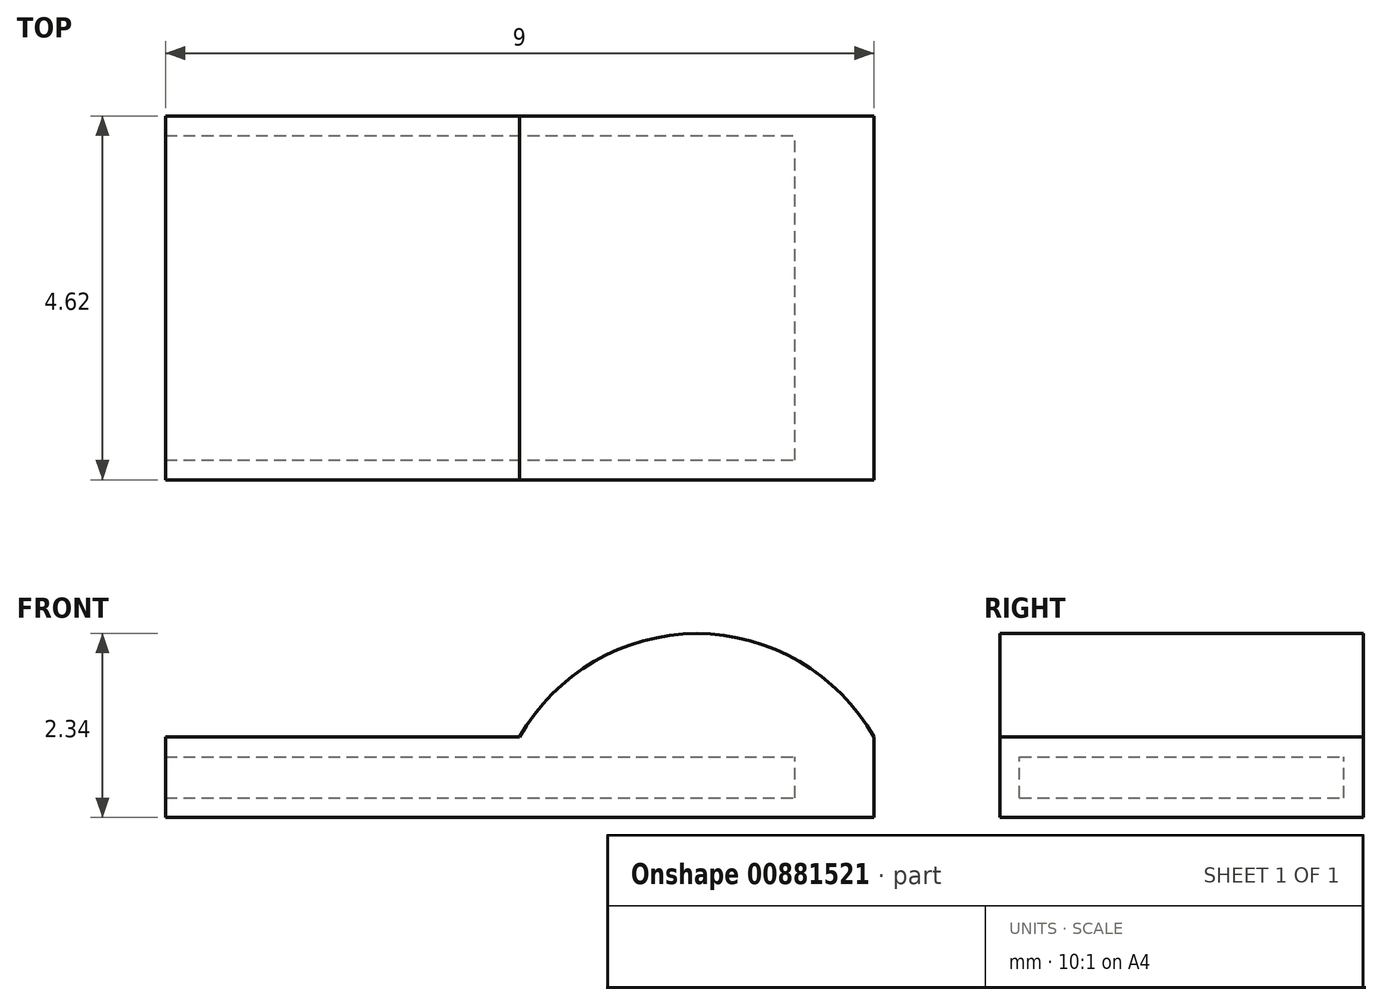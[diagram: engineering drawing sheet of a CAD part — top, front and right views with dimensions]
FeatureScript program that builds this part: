
annotation { "Feature Type Name" : "Feature", "Feature Type Description" : "" }
export const myFeature = defineFeature(function(context is Context, id is Id, definition is map)
    precondition{}
    {
        {
            var Q0;
            Q0=qCreatedBy(makeId("Right.planeOp"),FACE);
            var sketch = newSketch(context, id + "F0", { "sketchPlane" : qUnion([Q0])});
            skLineSegment(sketch, "E0.0", {"start": v(5.37, 19.45) * mm, "end": v(5.37, 19.97) * mm});
            skLineSegment(sketch, "E0.1", {"start": v(1.25, 19.45) * mm, "end": v(5.37, 19.45) * mm});
            skLineSegment(sketch, "E0.2", {"start": v(1.25, 19.45) * mm, "end": v(1.25, 19.97) * mm});
            skLineSegment(sketch, "E0.3", {"start": v(1.25, 19.97) * mm, "end": v(5.37, 19.97) * mm});
            skLineSegment(sketch, "E1.0", {"start": v(5.62, 19.2) * mm, "end": v(5.62, 20.22) * mm});
            skLineSegment(sketch, "E1.1", {"start": v(1, 19.2) * mm, "end": v(5.62, 19.2) * mm});
            skLineSegment(sketch, "E1.2", {"start": v(1, 19.2) * mm, "end": v(1, 20.22) * mm});
            skLineSegment(sketch, "E1.3", {"start": v(1, 20.22) * mm, "end": v(5.62, 20.22) * mm});
            skSolve(sketch);
        }
        {
            var Q0;
            Q0 = qSketchRegion(id + "F0", true);
            extrude(context, id + "F1", {"entities" : qUnion([Q0]), "oppositeDirection" : true, "depth" : 8 * mm, "offsetDistance" : 25 * mm});
        }
        {
            var Q0;
            Q0=makeQuery(id+"F0.imprint","IMPRINT",FACE,{"disambiguationData":[TD([[makeQuery(id+"F0.imprint","IMPRINT",EDGE,{"derivedFrom":sQuery(id+"F0.wireOp",EDGE,"E0.0")}),-1.0]])]});
            var sketch = newSketch(context, id + "F2", { "sketchPlane" : qUnion([Q0])});
            skLineSegment(sketch, "E2.0", {"start": v(5.62, 19.2) * mm, "end": v(5.62, 20.22) * mm});
            skLineSegment(sketch, "E2.1", {"start": v(1, 19.2) * mm, "end": v(5.62, 19.2) * mm});
            skLineSegment(sketch, "E2.2", {"start": v(1, 19.2) * mm, "end": v(1, 20.22) * mm});
            skLineSegment(sketch, "E2.3", {"start": v(1, 20.22) * mm, "end": v(5.62, 20.22) * mm});
            skSolve(sketch);
        }
        {
            var Q0;
            Q0 = qSketchRegion(id + "F2", true);
            extrude(context, id + "F3", {"entities" : qUnion([Q0]), "operationType" : NewBodyOperationType.ADD, "depth" : 1 * mm, "offsetDistance" : 25 * mm});
        }
        {
            var Q0;
            Q0=makeQuery(id+"F1.opExtrude","SWEPT_FACE",FACE,{"disambiguationData":[OSD([sQuery(id+"F0.wireOp",EDGE,"E1.0")])]});
            var sketch = newSketch(context, id + "F4", { "sketchPlane" : qUnion([Q0])});
            skArc(sketch, "E3", {"start": v(3.5, 20.22) * mm, "mid": v(1.25, 21.54) * mm, "end": v(-1, 20.22) * mm});
            skSolve(sketch);
        }
        {
            var Q0;
            {var subQ0=sQuery(id+"F4.wireOp",EDGE,"E3");Q0=makeQuery(id+"F4.imprint","IMPRINT",FACE,{"disambiguationData":[TD([[makeQuery(id+"F4.imprint","IMPRINT",EDGE,{"derivedFrom":subQ0}),1.0]])]});}
            extrude(context, id + "F5", {"entities" : qUnion([Q0]), "operationType" : NewBodyOperationType.ADD, "oppositeDirection" : true, "depth" : 4.62 * mm, "offsetDistance" : 25 * mm});
        }
    });
